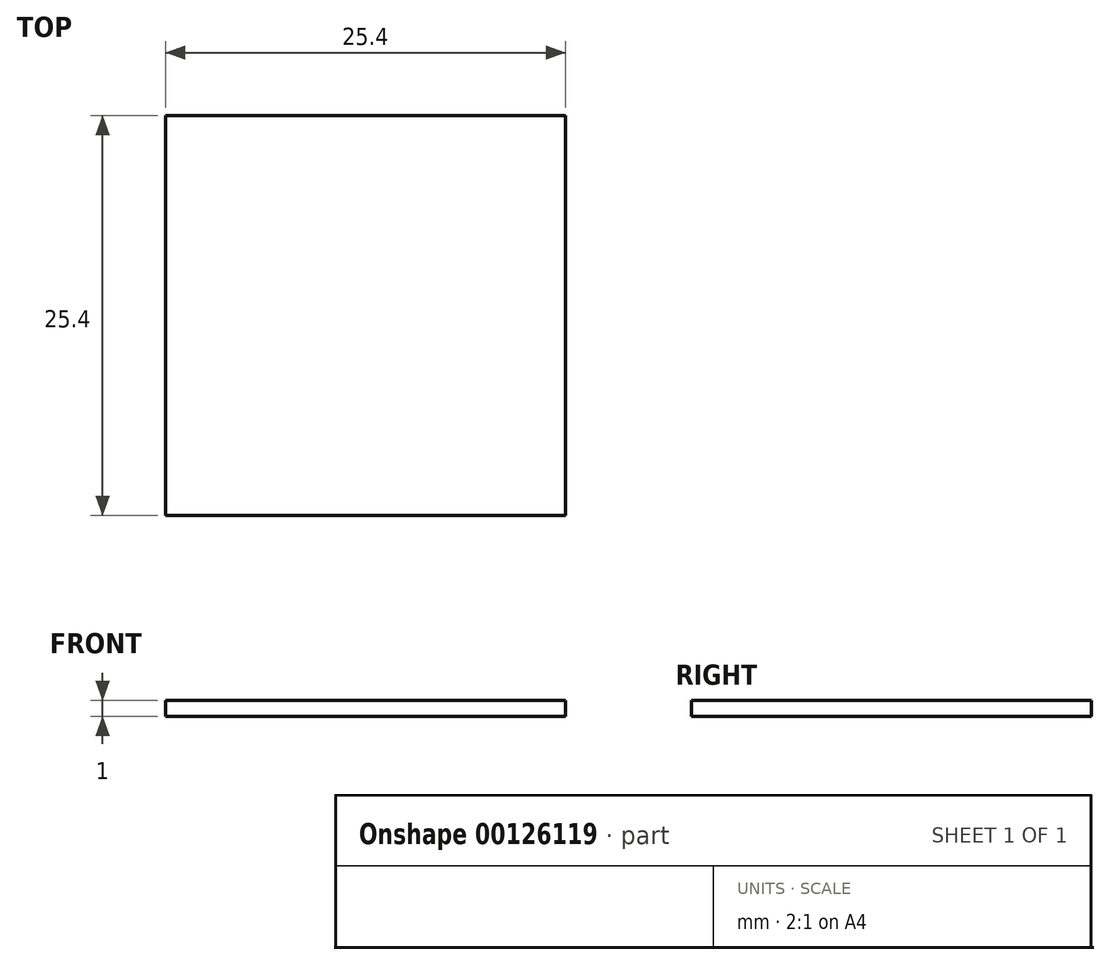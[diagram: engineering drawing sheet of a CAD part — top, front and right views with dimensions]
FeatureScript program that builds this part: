
annotation { "Feature Type Name" : "Feature", "Feature Type Description" : "" }
export const myFeature = defineFeature(function(context is Context, id is Id, definition is map)
    precondition{}
    {
        {
            var Q0;
            Q0=qCreatedBy(makeId("Top.planeOp"),FACE);
            var sketch = newSketch(context, id + "F0", { "sketchPlane" : qUnion([Q0])});
            skLineSegment(sketch, "E0.bottom", {"start": v(-17.75, 5.85) * mm, "end": v(7.65, 5.85) * mm});
            skLineSegment(sketch, "E0.top", {"start": v(-17.75, -19.55) * mm, "end": v(7.65, -19.55) * mm});
            skLineSegment(sketch, "E0.left", {"start": v(-17.75, 5.85) * mm, "end": v(-17.75, -19.55) * mm});
            skLineSegment(sketch, "E0.right", {"start": v(7.65, 5.85) * mm, "end": v(7.65, -19.55) * mm});
            skSolve(sketch);
        }
        {
            var Q0;
            Q0=makeQuery(id+"F0.imprint","IMPRINT",FACE,{"disambiguationData":[TD([[makeQuery(id+"F0.imprint","IMPRINT",EDGE,{"derivedFrom":sQuery(id+"F0.wireOp",EDGE,"E0.bottom")}),-1.0]])]});
            extrude(context, id + "F1", {"entities" : qUnion([Q0]), "depth" : 1 * mm});
        }
    });
